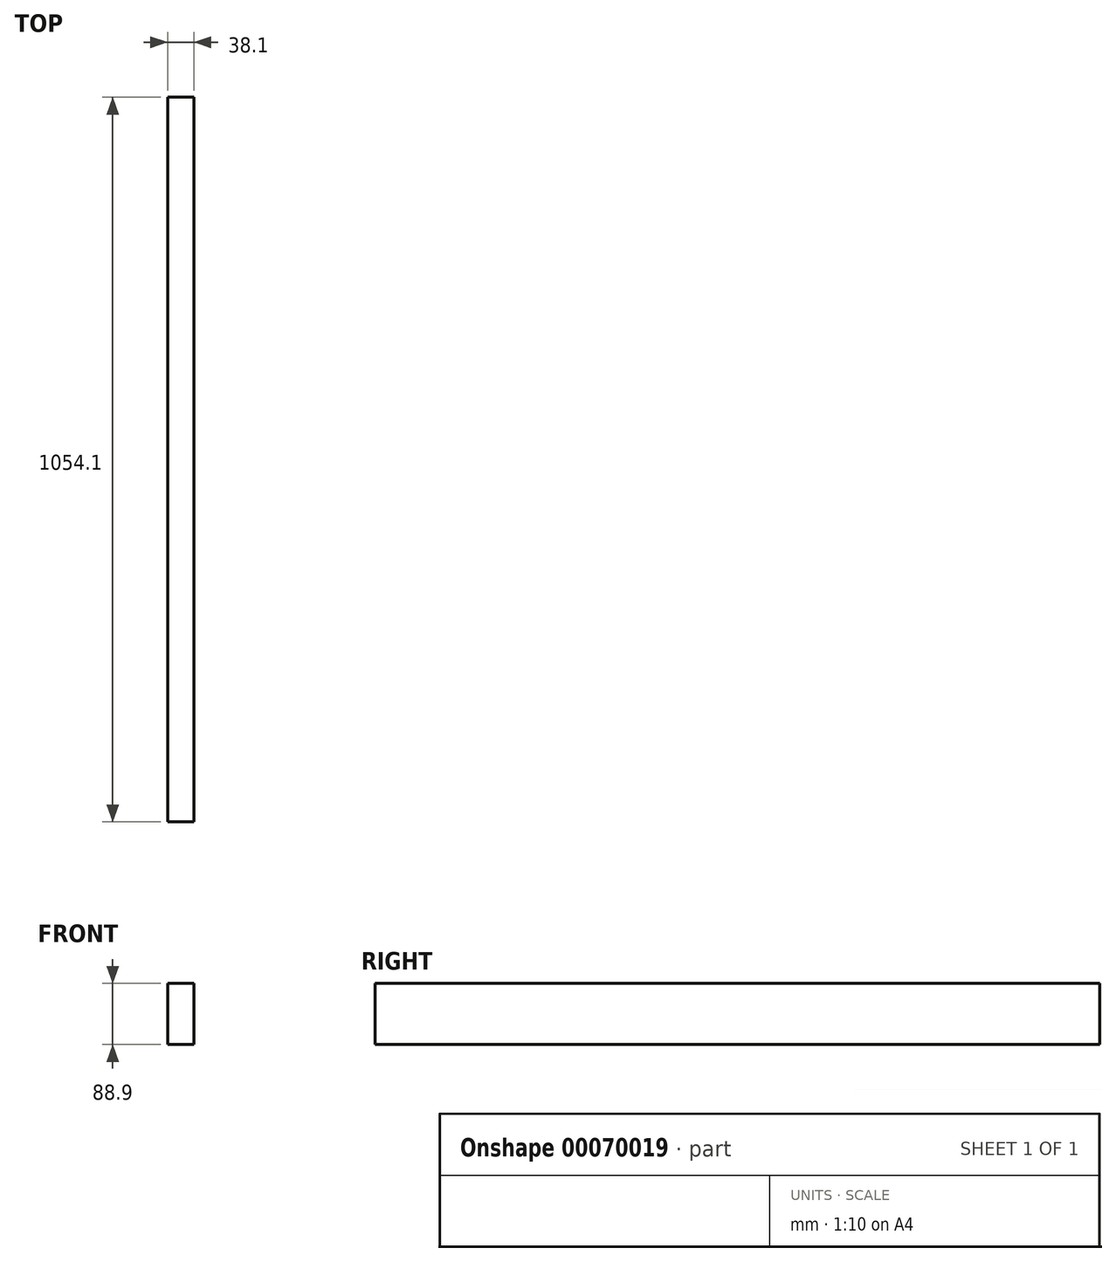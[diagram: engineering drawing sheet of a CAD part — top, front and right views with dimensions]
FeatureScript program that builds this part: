
annotation { "Feature Type Name" : "Feature", "Feature Type Description" : "" }
export const myFeature = defineFeature(function(context is Context, id is Id, definition is map)
    precondition{}
    {
        {
            var Q0;
            Q0=qCreatedBy(makeId("Top.planeOp"),FACE);
            var sketch = newSketch(context, id + "F0", { "sketchPlane" : qUnion([Q0])});
            skLineSegment(sketch, "E0.bottom", {"start": v(0, 0) * mm, "end": v(38.1, 0) * mm});
            skLineSegment(sketch, "E0.top", {"start": v(0, 1054.1) * mm, "end": v(38.1, 1054.1) * mm});
            skLineSegment(sketch, "E0.left", {"start": v(0, 0) * mm, "end": v(0, 1054.1) * mm});
            skLineSegment(sketch, "E0.right", {"start": v(38.1, 0) * mm, "end": v(38.1, 1054.1) * mm});
            skSolve(sketch);
        }
        {
            var Q0;
            Q0 = qSketchRegion(id + "F0", true);
            extrude(context, id + "F1", {"entities" : qUnion([Q0]), "depth" : 88.9 * mm});
        }
    });
